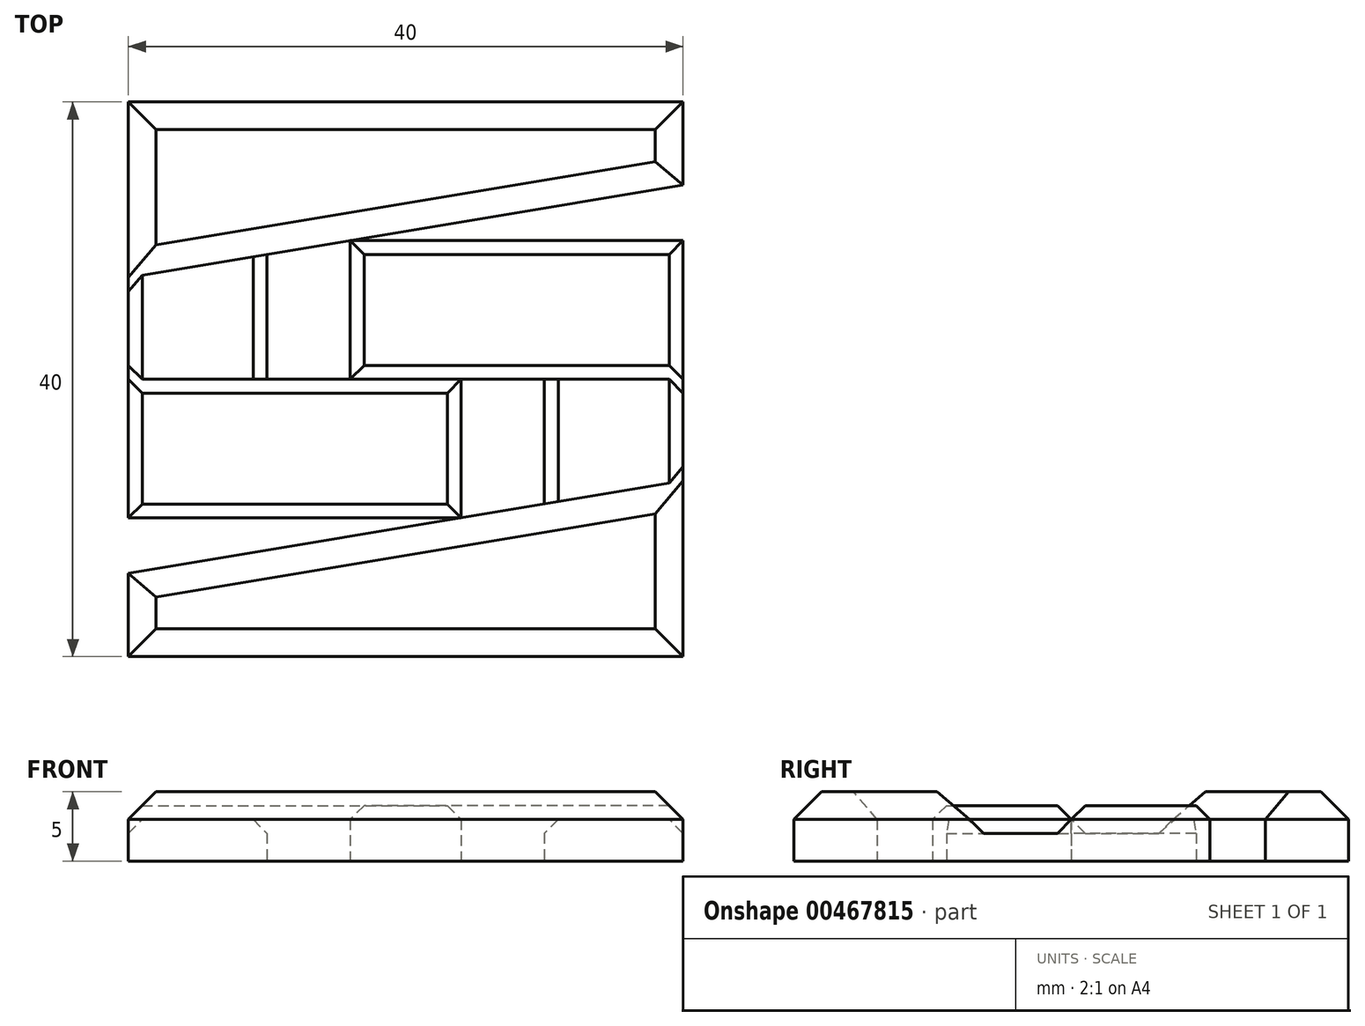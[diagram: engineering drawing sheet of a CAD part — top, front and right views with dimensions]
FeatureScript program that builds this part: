
annotation { "Feature Type Name" : "Feature", "Feature Type Description" : "" }
export const myFeature = defineFeature(function(context is Context, id is Id, definition is map)
    precondition{}
    {
        {
            var Q0;
            Q0=qCreatedBy(makeId("Top.planeOp"),FACE);
            var sketch = newSketch(context, id + "F0", { "sketchPlane" : qUnion([Q0])});
            skLineSegment(sketch, "E0", {"start": v(-20, 20) * mm, "end": v(20, 20) * mm});
            skLineSegment(sketch, "E1", {"start": v(20, 20) * mm, "end": v(20, 14) * mm});
            skLineSegment(sketch, "E2", {"start": v(20, 14) * mm, "end": v(-20, 7.33) * mm});
            skLineSegment(sketch, "E3", {"start": v(-20, 7.33) * mm, "end": v(-20, 20) * mm});
            skLineSegment(sketch, "E4", {"start": v(-20, 7.33) * mm, "end": v(-20, 0) * mm});
            skLineSegment(sketch, "E5", {"start": v(-20, 0) * mm, "end": v(-10, 0) * mm});
            skLineSegment(sketch, "E6", {"start": v(-10, 0) * mm, "end": v(-10, 9) * mm});
            skLineSegment(sketch, "E7", {"start": v(-20, 0) * mm, "end": v(-20, -10) * mm});
            skLineSegment(sketch, "E8", {"start": v(-20, -10) * mm, "end": v(4, -10) * mm});
            skLineSegment(sketch, "E9", {"start": v(4, -10) * mm, "end": v(4, 0) * mm});
            skLineSegment(sketch, "E10", {"start": v(4, 0) * mm, "end": v(-10, 0) * mm});
            skSolve(sketch);
        }
        {
            var Q0;
            Q0=makeQuery(id+"F0.imprint","IMPRINT",FACE,{"disambiguationData":[TD([[makeQuery(id+"F0.imprint","IMPRINT",EDGE,{"derivedFrom":sQuery(id+"F0.wireOp",EDGE,"E0")}),-1.0]])]});
            extrude(context, id + "F1", {"entities" : qUnion([Q0]), "depth" : 5 * mm});
        }
        {
            var Q0;
            Q0=makeQuery(id+"F0.imprint","IMPRINT",FACE,{"disambiguationData":[TD([[makeQuery(id+"F0.imprint","IMPRINT",EDGE,{"derivedFrom":sQuery(id+"F0.wireOp",EDGE,"E5")}),-1.0]])]});
            extrude(context, id + "F2", {"entities" : qUnion([Q0]), "depth" : 4 * mm});
        }
        {
            var Q0;
            {var subQ0=sQuery(id+"F0.wireOp",EDGE,"E4");Q0=makeQuery(id+"F0.imprint","IMPRINT",FACE,{"disambiguationData":[TD([[makeQuery(id+"F0.imprint","IMPRINT",EDGE,{"derivedFrom":subQ0}),1.0]])]});}
            extrude(context, id + "F3", {"entities" : qUnion([Q0]), "operationType" : NewBodyOperationType.ADD, "depth" : 3 * mm});
        }
        {
            var Q0;
            Q0=makeQuery(id+"F1.opExtrude","CAP_FACE",FACE,{"disambiguationData":[OSD([sQuery(id+"F0.wireOp",EDGE,"E0"),sQuery(id+"F0.wireOp",EDGE,"E1"),sQuery(id+"F0.wireOp",EDGE,"E2"),sQuery(id+"F0.wireOp",EDGE,"E3")])],"isStart":false});
            chamfer(context, id + "F4", {"entities" : qUnion([Q0]), "width" : 2 * mm, "tangentPropagation" : true});
        }
        {
            var Q0;
            Q0=makeQuery(id+"F2.opExtrude","CAP_FACE",FACE,{"disambiguationData":[OSD([sQuery(id+"F0.wireOp",EDGE,"E5"),sQuery(id+"F0.wireOp",EDGE,"E7"),sQuery(id+"F0.wireOp",EDGE,"E8"),sQuery(id+"F0.wireOp",EDGE,"E9"),sQuery(id+"F0.wireOp",EDGE,"E10")])],"isStart":false});
            chamfer(context, id + "F5", {"entities" : qUnion([Q0]), "width" : 1 * mm, "tangentPropagation" : true});
        }
        {
            var Q0;
            Q0=makeQuery(id+"F3.opExtrude","CAP_EDGE",EDGE,{"disambiguationData":[OSD([sQuery(id+"F0.wireOp",EDGE,"E6")])],"isStart":false});
            var Q1;
            Q1=makeQuery(id+"F3.opExtrude","CAP_EDGE",EDGE,{"disambiguationData":[OSD([sQuery(id+"F0.wireOp",EDGE,"E4")])],"isStart":false});
            chamfer(context, id + "F6", {"entities" : qUnion([Q0, Q1]), "width" : 1 * mm, "tangentPropagation" : true});
        }
        {
            var Q0;
            Q0=qCreatedBy(makeId("Right.planeOp"),FACE);
            var sketch = newSketch(context, id + "F7", { "sketchPlane" : qUnion([Q0])});
            skLineSegment(sketch, "E11", {"start": v(0, 26.12) * mm, "end": v(0, -30.23) * mm});
            skSolve(sketch);
        }
        {
            var Q0;
            Q0=makeQuery(id+"F1.opExtrude","SWEPT_BODY",BODY,{"disambiguationData":[OSD([sQuery(id+"F0.wireOp",EDGE,"E0"),sQuery(id+"F0.wireOp",EDGE,"E1"),sQuery(id+"F0.wireOp",EDGE,"E2"),sQuery(id+"F0.wireOp",EDGE,"E3")])]});
            var Q1;
            Q1=sQuery(id+"F7.wireOp",EDGE,"E11");
            circularPattern(context, id + "F8", {"entities" : qUnion([Q0]), "axis" : qUnion([Q1]), "angle" : 360 * degree, "instanceCount" : 2, "equalSpace" : true});
        }
    });
